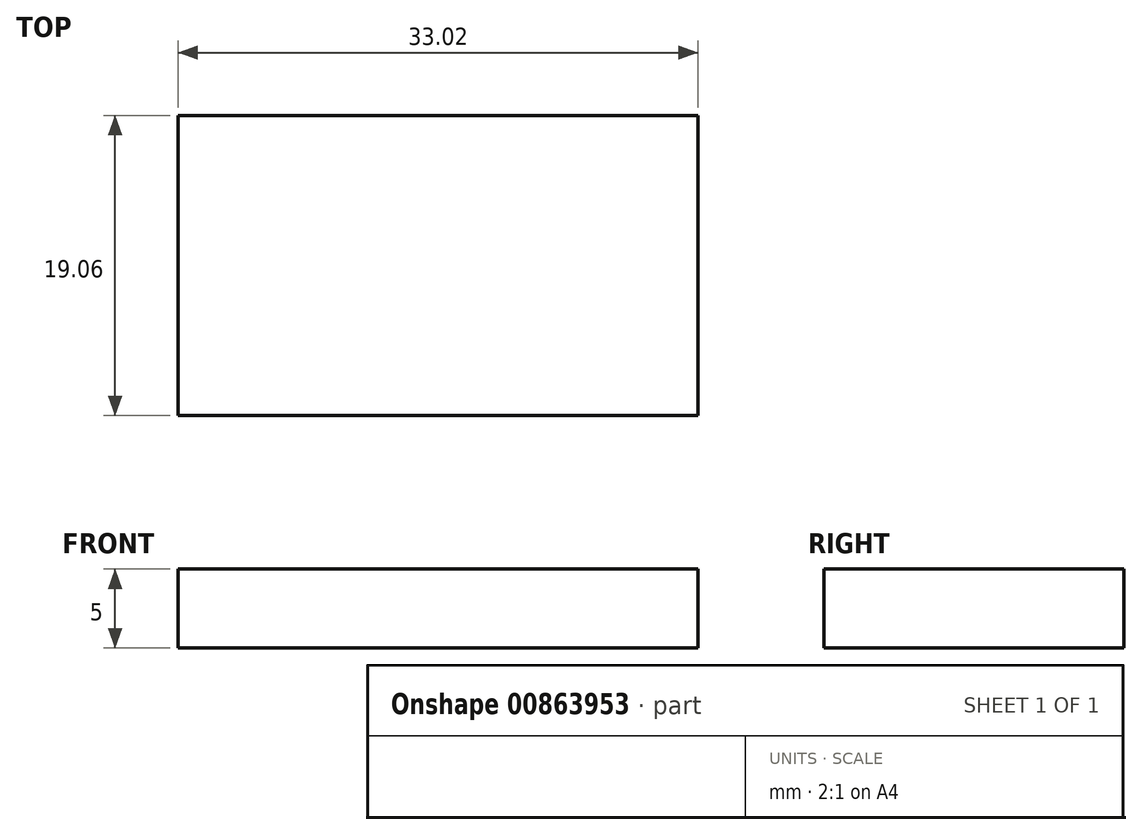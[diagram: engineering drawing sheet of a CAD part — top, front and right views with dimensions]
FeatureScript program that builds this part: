
annotation { "Feature Type Name" : "Feature", "Feature Type Description" : "" }
export const myFeature = defineFeature(function(context is Context, id is Id, definition is map)
    precondition{}
    {
        {
            var Q0;
            Q0=qCreatedBy(makeId("Top.planeOp"),FACE);
            var sketch = newSketch(context, id + "F0", { "sketchPlane" : qUnion([Q0])});
            skLineSegment(sketch, "E0.bottom", {"start": v(-16.51, 9.53) * mm, "end": v(16.51, 9.53) * mm});
            skLineSegment(sketch, "E0.top", {"start": v(-16.51, -9.53) * mm, "end": v(16.51, -9.53) * mm});
            skLineSegment(sketch, "E0.left", {"start": v(-16.51, 9.53) * mm, "end": v(-16.51, -9.53) * mm});
            skLineSegment(sketch, "E0.right", {"start": v(16.51, 9.53) * mm, "end": v(16.51, -9.53) * mm});
            skLineSegment(sketch, "E1", {"start": v(-16.51, 9.53) * mm, "end": v(16.51, -9.52) * mm, "construction": true});
            skSolve(sketch);
        }
        {
            var Q0;
            Q0 = qSketchRegion(id + "F0", true);
            extrude(context, id + "F1", {"entities" : qUnion([Q0]), "depth" : 5 * mm, "offsetDistance" : 25 * mm});
        }
    });
